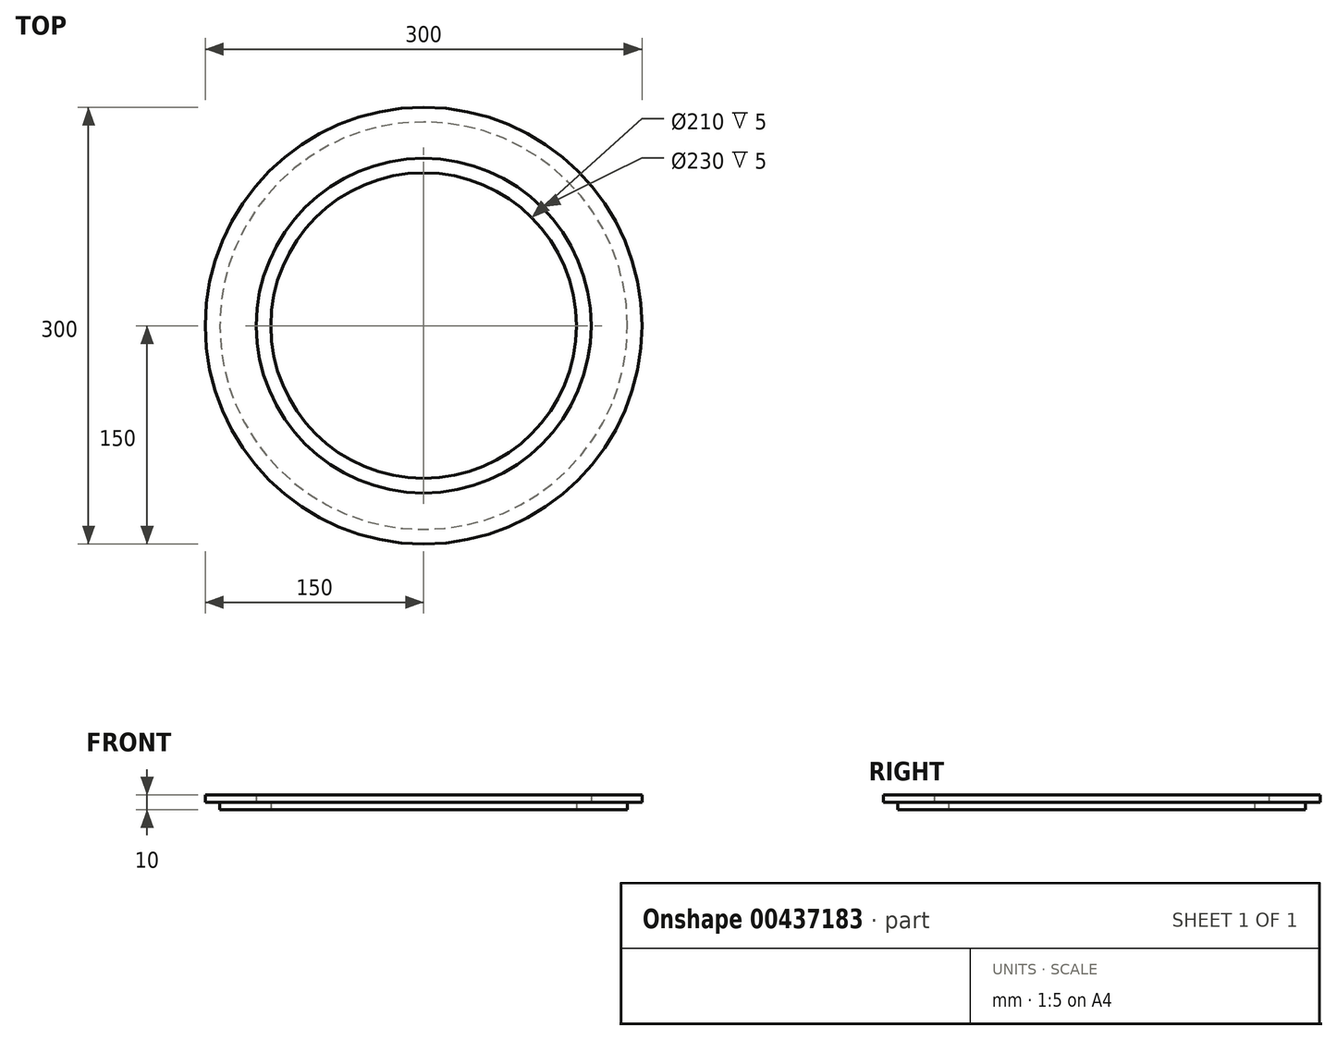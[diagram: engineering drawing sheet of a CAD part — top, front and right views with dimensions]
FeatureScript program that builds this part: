
annotation { "Feature Type Name" : "Feature", "Feature Type Description" : "" }
export const myFeature = defineFeature(function(context is Context, id is Id, definition is map)
    precondition{}
    {
        {
            var Q0;
            Q0=qCreatedBy(makeId("Front.planeOp"),FACE);
            var sketch = newSketch(context, id + "F0", { "sketchPlane" : qUnion([Q0])});
            skLineSegment(sketch, "E0", {"start": v(105, 0) * mm, "end": v(140, 0) * mm});
            skLineSegment(sketch, "E1", {"start": v(140, 0) * mm, "end": v(140, 5) * mm});
            skLineSegment(sketch, "E2", {"start": v(140, 5) * mm, "end": v(150, 5) * mm});
            skLineSegment(sketch, "E3", {"start": v(150, 5) * mm, "end": v(150, 10) * mm});
            skLineSegment(sketch, "E4", {"start": v(150, 10) * mm, "end": v(115, 10) * mm});
            skLineSegment(sketch, "E5", {"start": v(115, 10) * mm, "end": v(115, 5) * mm});
            skLineSegment(sketch, "E6", {"start": v(115, 5) * mm, "end": v(105, 5) * mm});
            skLineSegment(sketch, "E7", {"start": v(105, 5) * mm, "end": v(105, 0) * mm});
            skLineSegment(sketch, "E8", {"start": v(0, 0) * mm, "end": v(0, 115.63) * mm, "construction": true});
            skSolve(sketch);
        }
        {
            var Q0;
            Q0=makeQuery(id+"F0.imprint","IMPRINT",FACE,{"disambiguationData":[TD([[makeQuery(id+"F0.imprint","IMPRINT",EDGE,{"derivedFrom":sQuery(id+"F0.wireOp",EDGE,"E0")}),1.0]])]});
            var Q1;
            Q1=sQuery(id+"F0.wireOp",EDGE,"E8");
            var Q2;
            Q2=sQuery(id+"F0.wireOp",EDGE,"E8");
            revolve(context, id + "F1", {"entities" : qUnion([Q0]), "surfaceEntities" : qUnion([Q1]), "axis" : qUnion([Q2]), "revolveType" : RevolveType.FULL});
        }
    });
